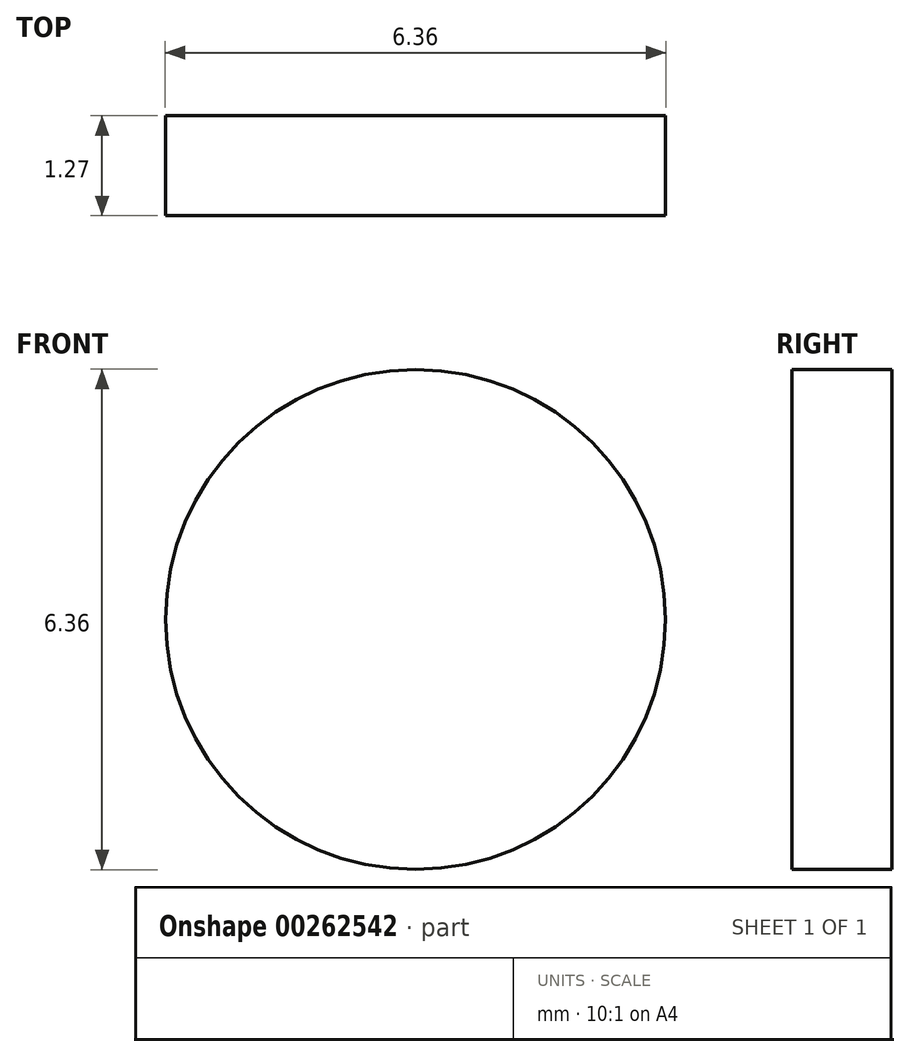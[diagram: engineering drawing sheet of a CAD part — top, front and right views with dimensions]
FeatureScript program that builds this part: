
annotation { "Feature Type Name" : "Feature", "Feature Type Description" : "" }
export const myFeature = defineFeature(function(context is Context, id is Id, definition is map)
    precondition{}
    {
        {
            var Q0;
            Q0=qCreatedBy(makeId("Front.planeOp"),FACE);
            var sketch = newSketch(context, id + "F0", { "sketchPlane" : qUnion([Q0])});
            skCircle(sketch, "E0", {"center": v(0, 0) * mm, "radius": 3.18 * mm});
            skSolve(sketch);
        }
        {
            var Q0;
            Q0=makeQuery(id+"F0.imprint","IMPRINT",FACE,{"disambiguationData":[TD([[makeQuery(id+"F0.imprint","IMPRINT",EDGE,{"derivedFrom":sQuery(id+"F0.wireOp",EDGE,"E0")}),1.0]])]});
            extrude(context, id + "F1", {"entities" : qUnion([Q0]), "depth" : 1.27 * mm});
        }
    });
